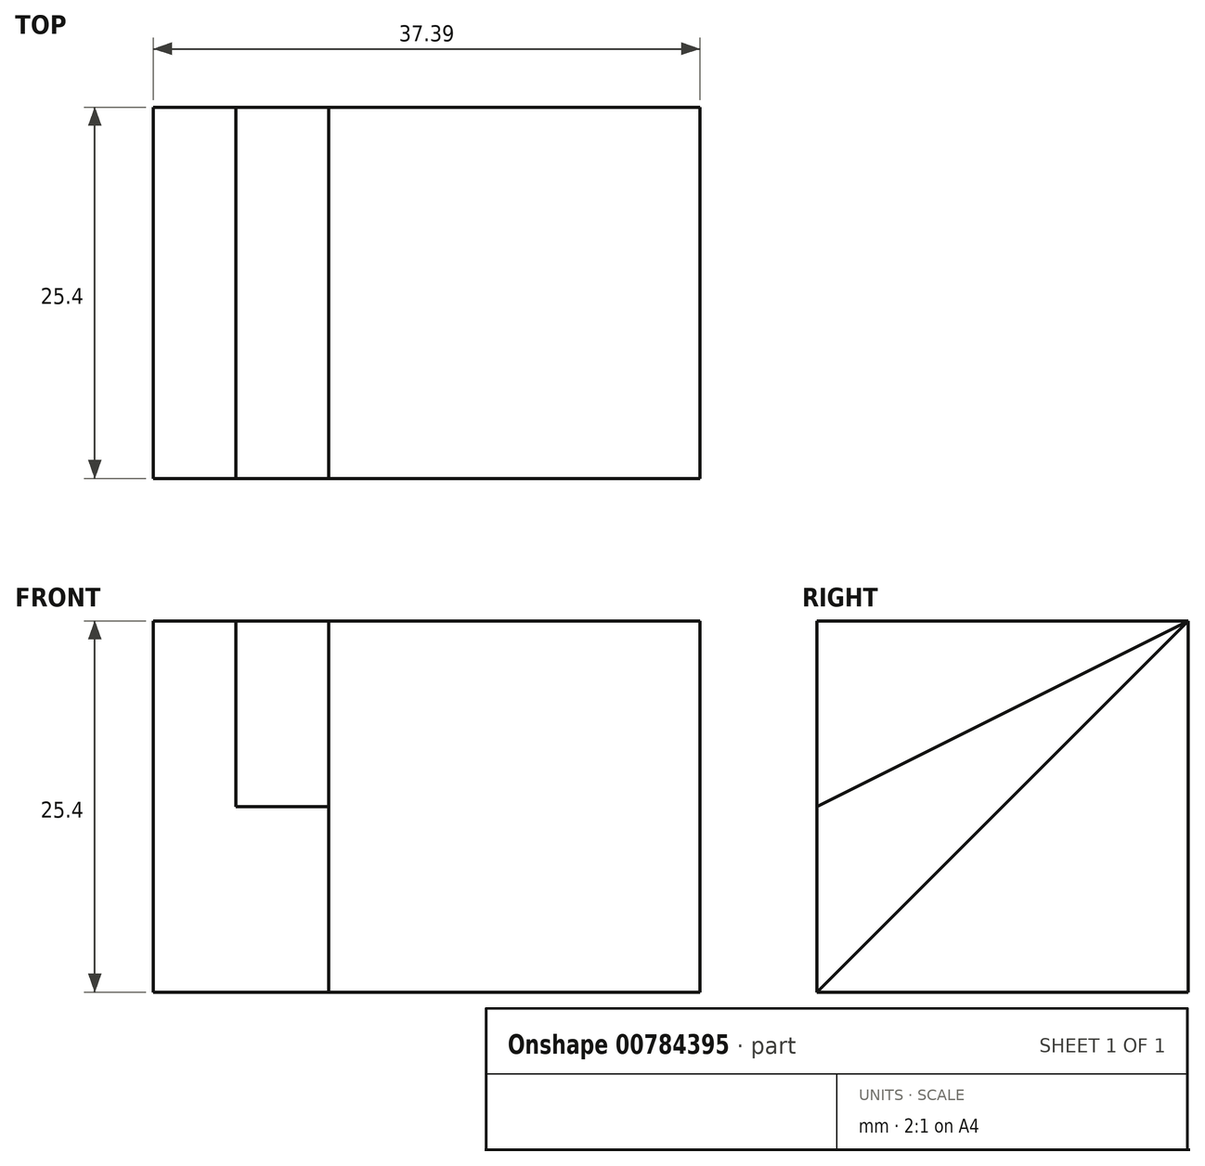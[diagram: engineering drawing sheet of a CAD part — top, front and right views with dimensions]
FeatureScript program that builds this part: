
annotation { "Feature Type Name" : "Feature", "Feature Type Description" : "" }
export const myFeature = defineFeature(function(context is Context, id is Id, definition is map)
    precondition{}
    {
        {
            var Q0;
            Q0=qCreatedBy(makeId("Front.planeOp"),FACE);
            var sketch = newSketch(context, id + "F0", { "sketchPlane" : qUnion([Q0])});
            skLineSegment(sketch, "E0", {"start": v(0, 0) * mm, "end": v(37.4, 0) * mm});
            skLineSegment(sketch, "E1", {"start": v(37.4, 0) * mm, "end": v(37.4, 25.4) * mm});
            skLineSegment(sketch, "E2", {"start": v(37.4, 25.4) * mm, "end": v(0, 25.4) * mm});
            skLineSegment(sketch, "E3", {"start": v(0, 0) * mm, "end": v(0, 25.4) * mm});
            skSolve(sketch);
        }
        {
            var Q0;
            Q0=makeQuery(id+"F0.imprint","IMPRINT",FACE,{"disambiguationData":[TD([[makeQuery(id+"F0.imprint","IMPRINT",EDGE,{"derivedFrom":sQuery(id+"F0.wireOp",EDGE,"E0")}),1.0]])]});
            extrude(context, id + "F1", {"entities" : qUnion([Q0]), "depth" : 25.4 * mm, "offsetDistance" : 25.4 * mm});
        }
        {
            var Q0;
            Q0=makeQuery(id+"F1.opExtrude","SWEPT_FACE",FACE,{"disambiguationData":[OSD([sQuery(id+"F0.wireOp",EDGE,"E1")])]});
            var sketch = newSketch(context, id + "F2", { "sketchPlane" : qUnion([Q0])});
            skLineSegment(sketch, "E4", {"start": v(-25.4, 0) * mm, "end": v(0, 25.4) * mm});
            skLineSegment(sketch, "E5", {"start": v(-25.4, 0) * mm, "end": v(-25.4, 25.4) * mm});
            skLineSegment(sketch, "E6", {"start": v(-25.4, 25.4) * mm, "end": v(0, 25.4) * mm});
            skSolve(sketch);
        }
        {
            var Q0;
            Q0=makeQuery(id+"F2.imprint","IMPRINT",FACE,{"disambiguationData":[TD([[makeQuery(id+"F2.imprint","IMPRINT",EDGE,{"derivedFrom":sQuery(id+"F2.wireOp",EDGE,"E4")}),1.0]])]});
            extrude(context, id + "F3", {"entities" : qUnion([Q0]), "operationType" : NewBodyOperationType.REMOVE, "oppositeDirection" : true, "depth" : 25.4 * mm, "offsetDistance" : 25.4 * mm});
        }
        {
            var Q0;
            Q0=makeQuery(id+"F3.boolean.opBoolean","COPY",FACE,{"derivedFrom":makeQuery(id+"F3.opExtrude","CAP_FACE",FACE,{"disambiguationData":[OSD([sQuery(id+"F2.wireOp",EDGE,"E4"),sQuery(id+"F2.wireOp",EDGE,"E5"),sQuery(id+"F2.wireOp",EDGE,"E6")])],"isStart":false})});
            var sketch = newSketch(context, id + "F4", { "sketchPlane" : qUnion([Q0])});
            skLineSegment(sketch, "E7", {"start": v(-25.4, 0) * mm, "end": v(-25.4, 12.7) * mm});
            skLineSegment(sketch, "E8", {"start": v(-25.4, 12.7) * mm, "end": v(0, 25.4) * mm});
            skLineSegment(sketch, "E9", {"start": v(-25.4, 12.7) * mm, "end": v(-25.4, 25.4) * mm});
            skLineSegment(sketch, "E10", {"start": v(-25.4, 25.4) * mm, "end": v(0, 25.4) * mm});
            skSolve(sketch);
        }
        {
            var Q0;
            Q0=makeQuery(id+"F4.imprint","IMPRINT",FACE,{"disambiguationData":[TD([[makeQuery(id+"F4.imprint","IMPRINT",EDGE,{"derivedFrom":sQuery(id+"F4.wireOp",EDGE,"E8")}),1.0]])]});
            extrude(context, id + "F5", {"entities" : qUnion([Q0]), "operationType" : NewBodyOperationType.REMOVE, "oppositeDirection" : true, "depth" : 6.35 * mm, "offsetDistance" : 25.4 * mm});
        }
    });
